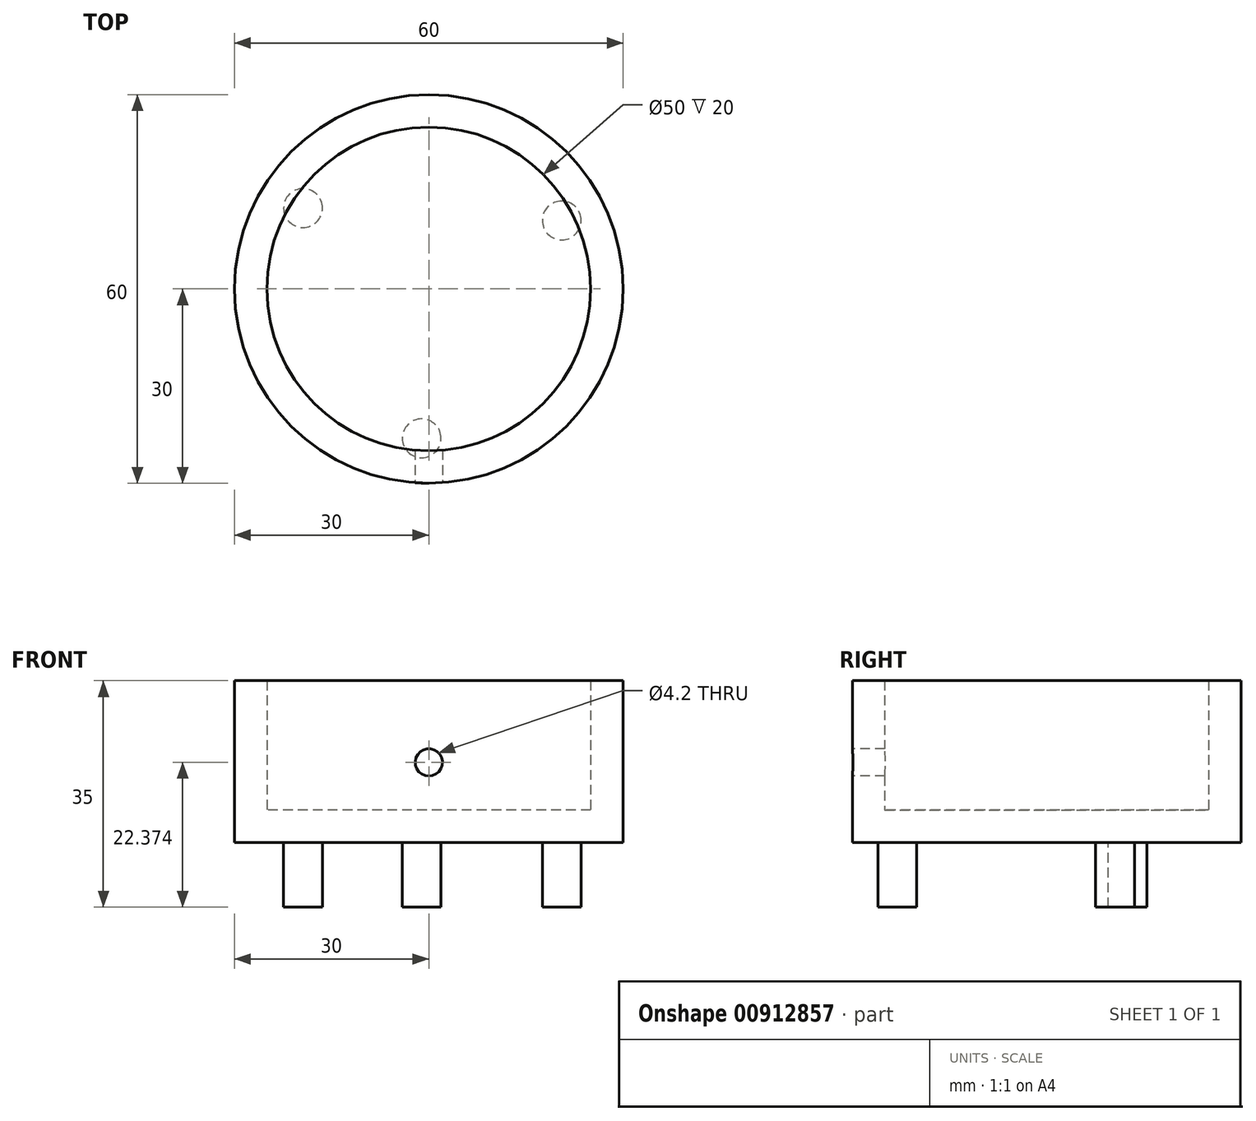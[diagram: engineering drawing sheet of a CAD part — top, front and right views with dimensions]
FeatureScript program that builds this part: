
annotation { "Feature Type Name" : "Feature", "Feature Type Description" : "" }
export const myFeature = defineFeature(function(context is Context, id is Id, definition is map)
    precondition{}
    {
        {
            var Q0;
            Q0=qCreatedBy(makeId("Top.planeOp"),FACE);
            var sketch = newSketch(context, id + "F0", { "sketchPlane" : qUnion([Q0])});
            skCircle(sketch, "E0", {"center": v(0, 0) * mm, "radius": 30 * mm});
            skCircle(sketch, "E1", {"center": v(0, 0) * mm, "radius": 25 * mm});
            skCircle(sketch, "E2.cCircle", {"center": v(0, 0) * mm, "radius": 11.55 * mm, "construction": true});
            skLineSegment(sketch, "E2.0", {"start": v(20.53, 10.57) * mm, "end": v(-1.1, -23.07) * mm});
            skLineSegment(sketch, "E2.1", {"start": v(-1.1, -23.07) * mm, "end": v(-19.42, 12.5) * mm});
            skLineSegment(sketch, "E2.2", {"start": v(-19.42, 12.5) * mm, "end": v(20.53, 10.57) * mm});
            skPoint(sketch, "E2.0.midPoint", {"position": v(9.71, -6.25) * mm});
            skLineSegment(sketch, "E3", {"start": v(-19.42, 12.5) * mm, "end": v(9.71, -6.25) * mm, "construction": true});
            skSolve(sketch);
        }
        {
            var Q0;
            Q0=makeQuery(id+"F0.imprint","IMPRINT",FACE,{"disambiguationData":[TD([[makeQuery(id+"F0.imprint","IMPRINT",EDGE,{"derivedFrom":sQuery(id+"F0.wireOp",EDGE,"E0")}),1.0]])]});
            extrude(context, id + "F1", {"entities" : qUnion([Q0]), "depth" : 25 * mm, "offsetDistance" : 25 * mm});
        }
        {
            var Q0;
            Q0=qCreatedBy(makeId("Top.planeOp"),FACE);
            var sketch = newSketch(context, id + "F2", { "sketchPlane" : qUnion([Q0])});
            skCircle(sketch, "E4", {"center": v(0, 0) * mm, "radius": 30 * mm});
            skSolve(sketch);
        }
        {
            var Q0;
            Q0=makeQuery(id+"F2.imprint","IMPRINT",FACE,{"disambiguationData":[TD([[makeQuery(id+"F2.imprint","IMPRINT",EDGE,{"derivedFrom":sQuery(id+"F2.wireOp",EDGE,"E4")}),1.0]])]});
            extrude(context, id + "F3", {"entities" : qUnion([Q0]), "operationType" : NewBodyOperationType.ADD, "depth" : 5 * mm, "offsetDistance" : 25 * mm});
        }
        {
            var Q0;
            Q0=makeQuery(id+"F0.imprint","IMPRINT",FACE,{"disambiguationData":[TD([[makeQuery(id+"F0.imprint","IMPRINT",EDGE,{"derivedFrom":sQuery(id+"F0.wireOp",EDGE,"E2.0")}),-1.0]])]});
            var sketch = newSketch(context, id + "F4", { "sketchPlane" : qUnion([Q0])});
            skCircle(sketch, "E5", {"center": v(-1.1, -23.07) * mm, "radius": 3 * mm});
            skCircle(sketch, "E6", {"center": v(-19.42, 12.5) * mm, "radius": 3 * mm});
            skCircle(sketch, "E7", {"center": v(20.53, 10.57) * mm, "radius": 3 * mm});
            skSolve(sketch);
        }
        {
            var Q0;
            Q0 = qSketchRegion(id + "F4", true);
            extrude(context, id + "F5", {"entities" : qUnion([Q0]), "operationType" : NewBodyOperationType.ADD, "depth" : -10 * mm, "offsetDistance" : 25 * mm});
        }
        {
            var Q0;
            Q0=qCreatedBy(makeId("Front.planeOp"),FACE);
            cPlane(context, id + "F6", {"entities" : qUnion([Q0]), "cplaneType" : CPlaneType.OFFSET, "offset" : 30 * mm, "width" : 150 * mm, "height" : 150 * mm});
        }
        {
            var Q0;
            Q0=qCreatedBy(makeId("Front.planeOp"),FACE);
            var sketch = newSketch(context, id + "F7", { "sketchPlane" : qUnion([Q0])});
            skPoint(sketch, "E8", {"position": v(0, 24.75) * mm});
            skPoint(sketch, "E9", {"position": v(0, 12.37) * mm});
            skSolve(sketch);
        }
        {
            var Q0;
            Q0=qCreatedBy(id+"F6.planeOp",FACE);
            var sketch = newSketch(context, id + "F8", { "sketchPlane" : qUnion([Q0])});
            skCircle(sketch, "E10", {"center": v(0, 12.37) * mm, "radius": 2.1 * mm});
            skSolve(sketch);
        }
        {
            var Q0;
            Q0=sQuery(id+"F8.wireOp",VERTEX,"E10.center");
            var Q1;
            Q1=makeQuery(id+"F1.opExtrude","SWEPT_BODY",BODY,{"disambiguationData":[OSD([sQuery(id+"F0.wireOp",EDGE,"E0"),sQuery(id+"F0.wireOp",EDGE,"E1")])]});
            hole(context, id + "F9", {"style" : HoleStyle.SIMPLE, "endStyle" : HoleEndStyle.BLIND, "holeDiameter" : 4.2 * mm, "majorDiameter" : 5 * mm, "holeDepth" : 12 * mm, "isTappedThrough" : true, "tappedDepth" : 12 * mm, "tapClearance" : 3, "locations" : qUnion([Q0]), "scope" : qUnion([Q1])});
        }
    });
